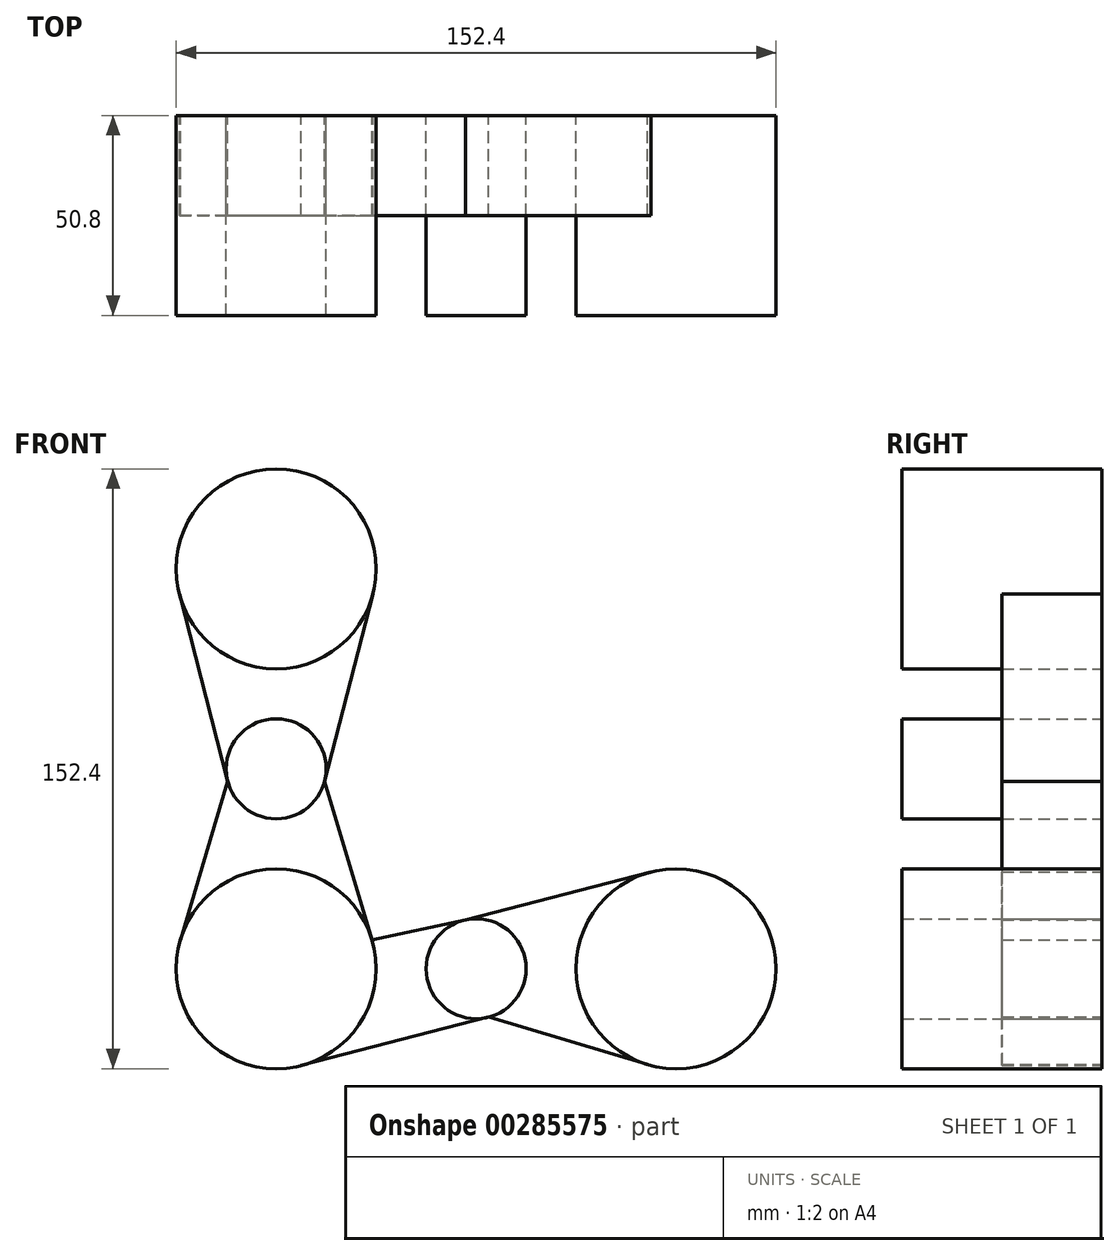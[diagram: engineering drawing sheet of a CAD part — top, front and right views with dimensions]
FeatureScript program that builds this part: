
annotation { "Feature Type Name" : "Feature", "Feature Type Description" : "" }
export const myFeature = defineFeature(function(context is Context, id is Id, definition is map)
    precondition{}
    {
        {
            var Q0;
            Q0=qCreatedBy(makeId("Front.planeOp"),FACE);
            var sketch = newSketch(context, id + "F0", { "sketchPlane" : qUnion([Q0])});
            skLineSegment(sketch, "E0", {"start": v(-75.24, -77.37) * mm, "end": v(-24.44, -77.37) * mm});
            skLineSegment(sketch, "E1", {"start": v(-75.24, -77.37) * mm, "end": v(-126.04, -77.37) * mm});
            skLineSegment(sketch, "E2", {"start": v(-126.04, -77.37) * mm, "end": v(-126.04, -26.57) * mm});
            skLineSegment(sketch, "E3", {"start": v(-126.04, -26.57) * mm, "end": v(-126.04, 24.23) * mm});
            skCircle(sketch, "E4", {"center": v(-126.04, 24.23) * mm, "radius": 25.4 * mm});
            skCircle(sketch, "E5", {"center": v(-126.04, -77.37) * mm, "radius": 25.4 * mm});
            skCircle(sketch, "E6", {"center": v(-24.44, -77.37) * mm, "radius": 25.4 * mm});
            skCircle(sketch, "E7", {"center": v(-75.24, -77.37) * mm, "radius": 12.7 * mm});
            skCircle(sketch, "E8", {"center": v(-126.04, -26.57) * mm, "radius": 12.7 * mm});
            skLineSegment(sketch, "E9", {"start": v(-150.63, 17.88) * mm, "end": v(-138.33, -29.75) * mm});
            skLineSegment(sketch, "E10", {"start": v(-101.44, 17.88) * mm, "end": v(-113.74, -29.75) * mm});
            skLineSegment(sketch, "E11", {"start": v(-138.33, -29.75) * mm, "end": v(-150.38, -70.11) * mm});
            skLineSegment(sketch, "E12", {"start": v(-113.74, -29.75) * mm, "end": v(-101.7, -70.11) * mm});
            skLineSegment(sketch, "E13", {"start": v(-101.7, -70.11) * mm, "end": v(-77.93, -64.96) * mm});
            skLineSegment(sketch, "E14", {"start": v(-77.93, -64.96) * mm, "end": v(-30.8, -52.78) * mm});
            skLineSegment(sketch, "E15", {"start": v(-119.69, -101.97) * mm, "end": v(-72.06, -89.67) * mm});
            skLineSegment(sketch, "E16", {"start": v(-72.06, -89.67) * mm, "end": v(-31.7, -101.71) * mm});
            skSolve(sketch);
        }
        {
            var Q0;
            {var subQ0=sQuery(id+"F0.wireOp",EDGE,"E4");var subQ1=makeQuery(id+"F0.imprint","INTERSECT",VERTEX,{"derivedFrom":[subQ0,sQuery(id+"F0.wireOp",EDGE,"E9")]});Q0=makeQuery(id+"F0.imprint","IMPRINT",FACE,{"disambiguationData":[TD([[makeQuery(id+"F0.imprint","IMPRINT",EDGE,{"disambiguationData":[TD([[subQ1,-1.0]])],"derivedFrom":subQ0}),1.0]])]});}
            var Q1;
            {var subQ3=sQuery(id+"F0.wireOp",EDGE,"E2");var subQ4=sQuery(id+"F0.wireOp",EDGE,"E1");var subQ5=makeQuery(id+"F0.imprint","INTERSECT",VERTEX,{"derivedFrom":[subQ4,subQ3]});Q1=makeQuery(id+"F0.imprint","IMPRINT",FACE,{"disambiguationData":[TD([[makeQuery(id+"F0.imprint","IMPRINT",EDGE,{"disambiguationData":[TD([[subQ5,1.0]])],"derivedFrom":subQ4}),1.0]])]});}
            var Q2;
            {var subQ0=sQuery(id+"F0.wireOp",EDGE,"E2");var subQ1=sQuery(id+"F0.wireOp",EDGE,"E1");var subQ2=makeQuery(id+"F0.imprint","INTERSECT",VERTEX,{"derivedFrom":[subQ1,subQ0]});Q2=makeQuery(id+"F0.imprint","IMPRINT",FACE,{"disambiguationData":[TD([[makeQuery(id+"F0.imprint","IMPRINT",EDGE,{"disambiguationData":[TD([[subQ2,1.0]])],"derivedFrom":subQ1}),-1.0]])]});}
            var Q3;
            {var subQ0=sQuery(id+"F0.wireOp",EDGE,"E3");var subQ1=sQuery(id+"F0.wireOp",EDGE,"E2");var subQ2=makeQuery(id+"F0.imprint","INTERSECT",VERTEX,{"derivedFrom":[subQ1,subQ0]});Q3=makeQuery(id+"F0.imprint","IMPRINT",FACE,{"disambiguationData":[TD([[makeQuery(id+"F0.imprint","IMPRINT",EDGE,{"disambiguationData":[TD([[subQ2,1.0]])],"derivedFrom":subQ1}),-1.0]])]});}
            var Q4;
            {var subQ0=sQuery(id+"F0.wireOp",EDGE,"E3");var subQ1=sQuery(id+"F0.wireOp",EDGE,"E2");var subQ2=makeQuery(id+"F0.imprint","INTERSECT",VERTEX,{"derivedFrom":[subQ1,subQ0]});Q4=makeQuery(id+"F0.imprint","IMPRINT",FACE,{"disambiguationData":[TD([[makeQuery(id+"F0.imprint","IMPRINT",EDGE,{"disambiguationData":[TD([[subQ2,1.0]])],"derivedFrom":subQ1}),1.0]])]});}
            var Q5;
            {var subQ0=sQuery(id+"F0.wireOp",EDGE,"E6");var subQ1=makeQuery(id+"F0.imprint","INTERSECT",VERTEX,{"derivedFrom":[subQ0,sQuery(id+"F0.wireOp",EDGE,"E14")]});Q5=makeQuery(id+"F0.imprint","IMPRINT",FACE,{"disambiguationData":[TD([[makeQuery(id+"F0.imprint","IMPRINT",EDGE,{"disambiguationData":[TD([[subQ1,-1.0]])],"derivedFrom":subQ0}),1.0]])]});}
            var Q6;
            {var subQ0=sQuery(id+"F0.wireOp",EDGE,"E1");var subQ1=sQuery(id+"F0.wireOp",EDGE,"E0");var subQ2=makeQuery(id+"F0.imprint","INTERSECT",VERTEX,{"derivedFrom":[subQ1,subQ0]});Q6=makeQuery(id+"F0.imprint","IMPRINT",FACE,{"disambiguationData":[TD([[makeQuery(id+"F0.imprint","IMPRINT",EDGE,{"disambiguationData":[TD([[subQ2,-1.0]])],"derivedFrom":subQ1}),1.0]])]});}
            var Q7;
            {var subQ0=sQuery(id+"F0.wireOp",EDGE,"E1");var subQ1=sQuery(id+"F0.wireOp",EDGE,"E0");var subQ2=makeQuery(id+"F0.imprint","INTERSECT",VERTEX,{"derivedFrom":[subQ1,subQ0]});Q7=makeQuery(id+"F0.imprint","IMPRINT",FACE,{"disambiguationData":[TD([[makeQuery(id+"F0.imprint","IMPRINT",EDGE,{"disambiguationData":[TD([[subQ2,-1.0]])],"derivedFrom":subQ1}),-1.0]])]});}
            extrude(context, id + "F1", {"entities" : qUnion([Q0, Q1, Q2, Q3, Q4, Q5, Q6, Q7]), "depth" : 50.8 * mm});
        }
        {
            var Q0;
            {var subQ5=sQuery(id+"F0.wireOp",EDGE,"E9");Q0=makeQuery(id+"F0.imprint","IMPRINT",FACE,{"disambiguationData":[TD([[makeQuery(id+"F0.imprint","IMPRINT",EDGE,{"derivedFrom":subQ5}),1.0]])]});}
            var Q1;
            {var subQ5=sQuery(id+"F0.wireOp",EDGE,"E10");Q1=makeQuery(id+"F0.imprint","IMPRINT",FACE,{"disambiguationData":[TD([[makeQuery(id+"F0.imprint","IMPRINT",EDGE,{"derivedFrom":subQ5}),-1.0]])]});}
            var Q2;
            {var subQ5=sQuery(id+"F0.wireOp",EDGE,"E11");Q2=makeQuery(id+"F0.imprint","IMPRINT",FACE,{"disambiguationData":[TD([[makeQuery(id+"F0.imprint","IMPRINT",EDGE,{"derivedFrom":subQ5}),1.0]])]});}
            var Q3;
            {var subQ5=sQuery(id+"F0.wireOp",EDGE,"E12");Q3=makeQuery(id+"F0.imprint","IMPRINT",FACE,{"disambiguationData":[TD([[makeQuery(id+"F0.imprint","IMPRINT",EDGE,{"derivedFrom":subQ5}),-1.0]])]});}
            var Q4;
            {var subQ5=sQuery(id+"F0.wireOp",EDGE,"E15");Q4=makeQuery(id+"F0.imprint","IMPRINT",FACE,{"disambiguationData":[TD([[makeQuery(id+"F0.imprint","IMPRINT",EDGE,{"derivedFrom":subQ5}),1.0]])]});}
            var Q5;
            {var subQ5=sQuery(id+"F0.wireOp",EDGE,"E13");Q5=makeQuery(id+"F0.imprint","IMPRINT",FACE,{"disambiguationData":[TD([[makeQuery(id+"F0.imprint","IMPRINT",EDGE,{"derivedFrom":subQ5}),-1.0]])]});}
            var Q6;
            {var subQ5=sQuery(id+"F0.wireOp",EDGE,"E14");Q6=makeQuery(id+"F0.imprint","IMPRINT",FACE,{"disambiguationData":[TD([[makeQuery(id+"F0.imprint","IMPRINT",EDGE,{"derivedFrom":subQ5}),-1.0]])]});}
            var Q7;
            {var subQ5=sQuery(id+"F0.wireOp",EDGE,"E16");Q7=makeQuery(id+"F0.imprint","IMPRINT",FACE,{"disambiguationData":[TD([[makeQuery(id+"F0.imprint","IMPRINT",EDGE,{"derivedFrom":subQ5}),1.0]])]});}
            extrude(context, id + "F2", {"entities" : qUnion([Q0, Q1, Q2, Q3, Q4, Q5, Q6, Q7]), "depth" : 25.4 * mm});
        }
    });
